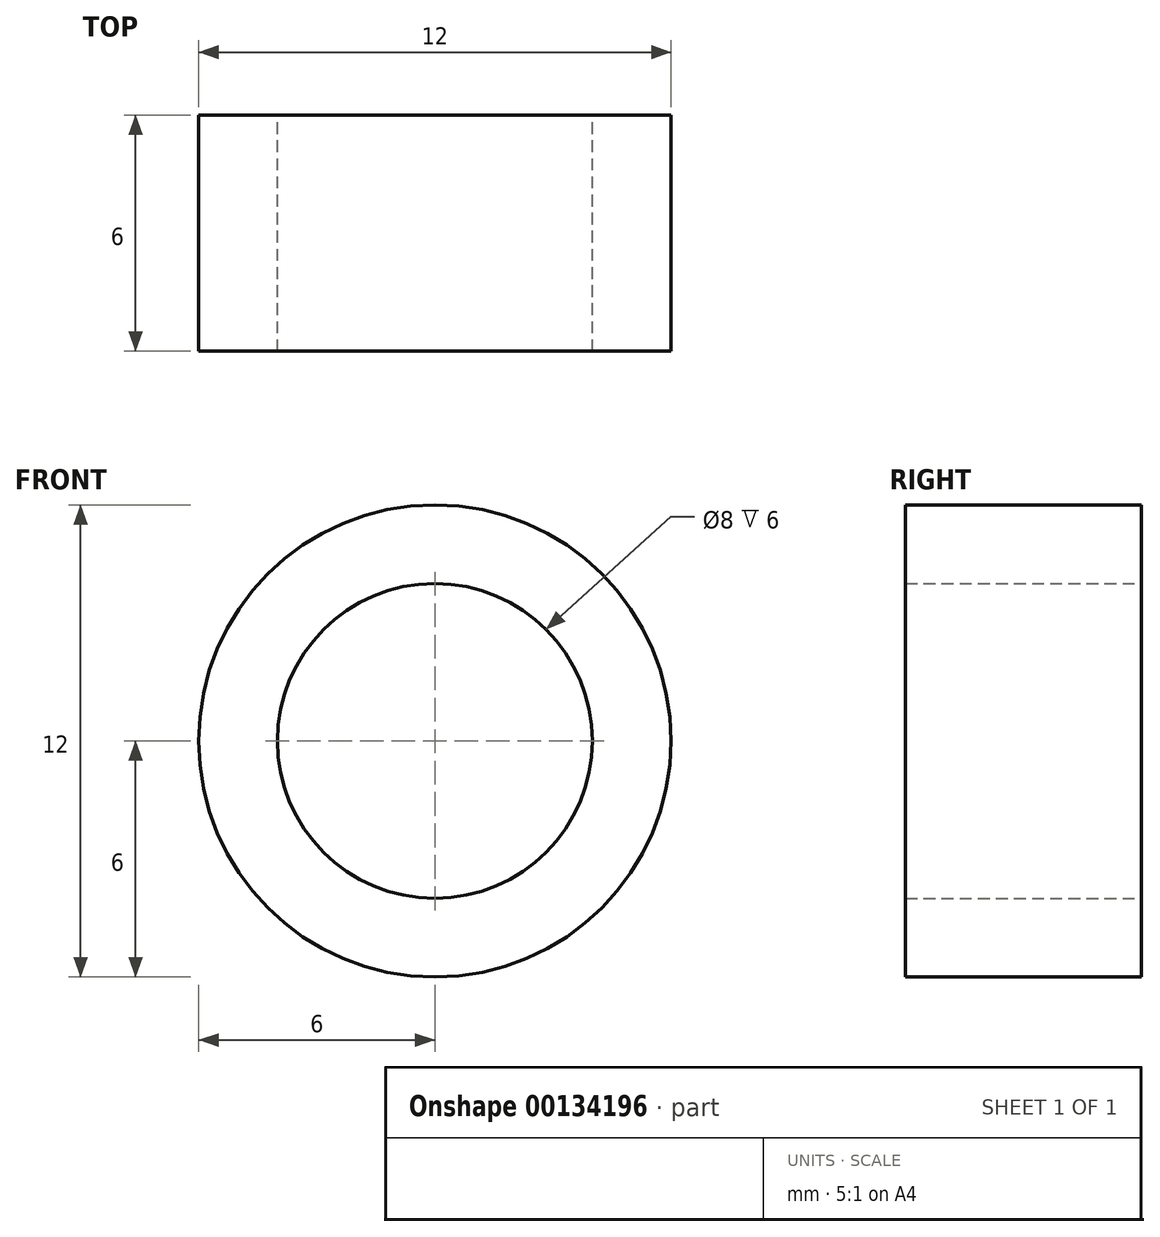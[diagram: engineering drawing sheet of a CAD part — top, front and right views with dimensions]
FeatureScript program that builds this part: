
annotation { "Feature Type Name" : "Feature", "Feature Type Description" : "" }
export const myFeature = defineFeature(function(context is Context, id is Id, definition is map)
    precondition{}
    {
        {
            var Q0;
            Q0=qCreatedBy(makeId("Front.planeOp"),FACE);
            var sketch = newSketch(context, id + "F0", { "sketchPlane" : qUnion([Q0])});
            skCircle(sketch, "E0", {"center": v(0, 0) * mm, "radius": 4 * mm});
            skCircle(sketch, "E1", {"center": v(0, 0) * mm, "radius": 6 * mm});
            skSolve(sketch);
        }
        {
            var Q0;
            Q0 = qSketchRegion(id + "F0", true);
            extrude(context, id + "F1", {"entities" : qUnion([Q0]), "depth" : 6 * mm});
        }
    });
